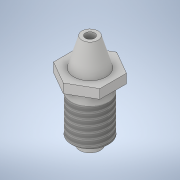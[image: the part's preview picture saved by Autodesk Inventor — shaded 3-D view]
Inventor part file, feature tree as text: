
AUTODESK INVENTOR PART (.ipt)
format: ipt  version: 2021 (Build 250183000, 183)  size: 139,776 bytes
history: native  units: mm
features: sketch x7, extrude x3, plane x2, loft x2, thread x1
ambient origin geometry x8: Origin, YZ Plane, XZ Plane, XY Plane, X Axis, Y Axis, Z Axis, Center Point
bodies: Solid1 (feature_tree)
feature tree (15):
  extrude  "Extrusion1"  Depth=2.0mm
  sketch  "Sketch2"  dims[d3=6.0mm d4=3.5mm]
  plane  "Work Plane1"
  loft  "Loft1"
  extrude  "Extrusion2"  TaperAngle=0.0deg  [1 undecoded]
  thread  "Thread1"  [1 undecoded]
  sketch  "Sketch5"  dims[d14=2.0mm d15=2.0mm]
  plane  "Work Plane2"
  loft  "Loft2"
  extrude  "Extrusion3"  Depth=2.0mm
  sketch  "Sketch1"  dims[d0=2.0mm d1=0.0mm d2=7.0mm]
  sketch  "Sketch3"  dims[d5=0.0mm d6=90.0deg d7=0.0mm d8=90.0deg d9=8.0mm]
  sketch  "Sketch4"  dims[d10=10.4mm d11=0.0mm d12=8.0mm d13=2.4mm]
  sketch  "Sketch6"  dims[d16=4.5mm]
  sketch  "Sketch7"  dims[d17=6.5mm d18=0.0mm d19=90.0deg d20=0.0mm d21=90.0deg d22=10.0mm d23=0.0mm d24=10.0mm]
note: 2 required parameter values undecoded (feature->parameter linkage not recoverable at this tier; creation-order binding heuristic only, values carry confidence <= 0.55)
